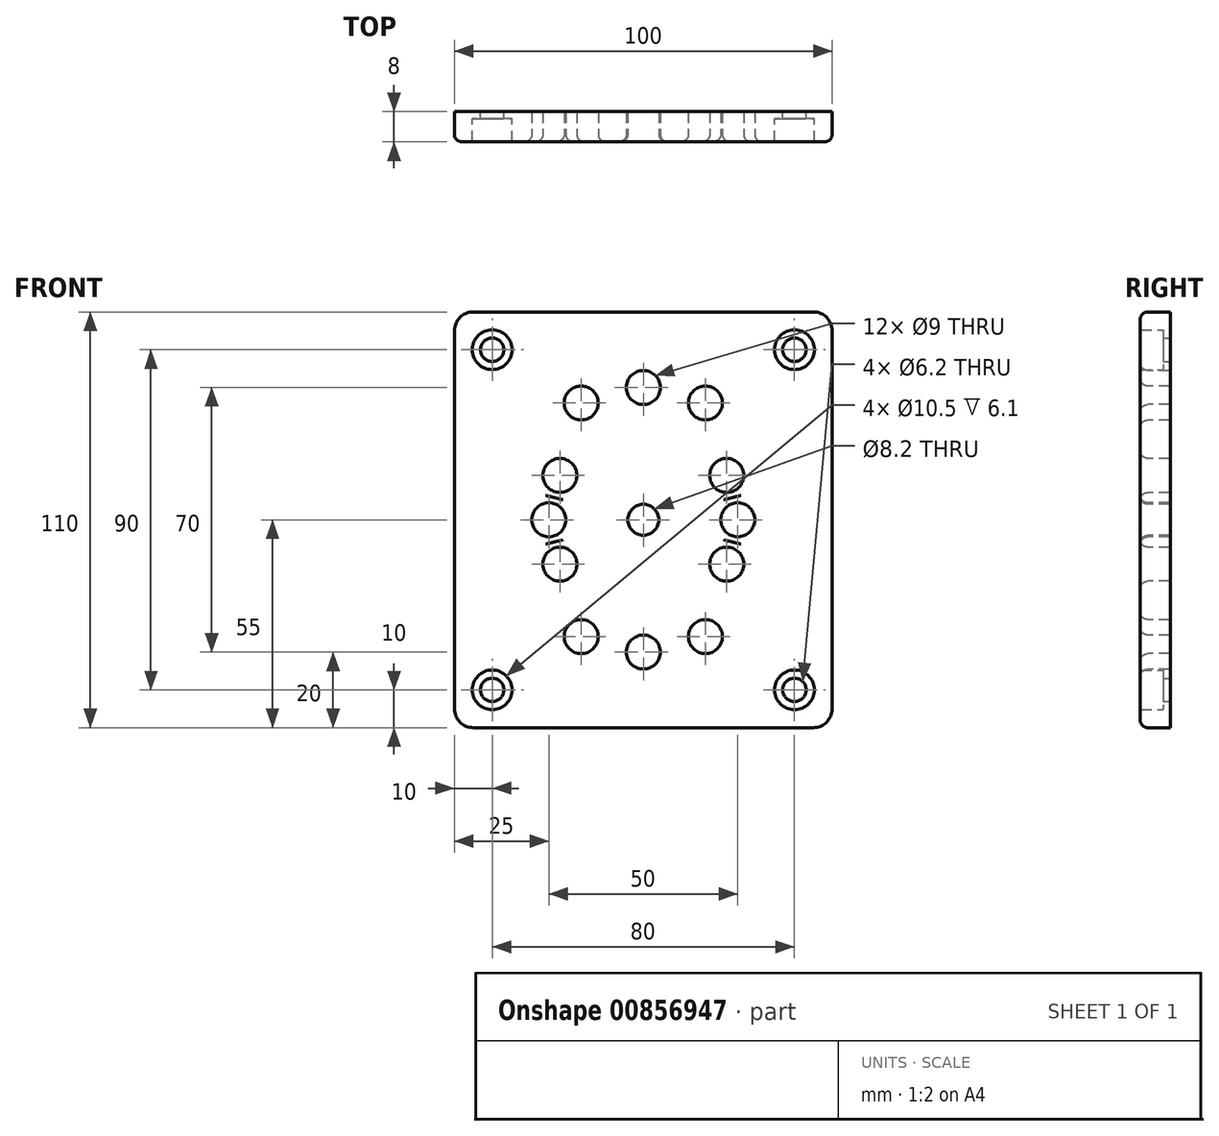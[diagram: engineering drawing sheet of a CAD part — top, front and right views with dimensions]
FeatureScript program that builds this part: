
annotation { "Feature Type Name" : "Feature", "Feature Type Description" : "" }
export const myFeature = defineFeature(function(context is Context, id is Id, definition is map)
    precondition{}
    {
        {
            var Q0;
            Q0=qCreatedBy(makeId("Front.planeOp"),FACE);
            var sketch = newSketch(context, id + "F0", { "sketchPlane" : qUnion([Q0])});
            skLineSegment(sketch, "E0.bottom", {"start": v(0, 0) * mm, "end": v(-100, 0) * mm});
            skLineSegment(sketch, "E0.top", {"start": v(0, 110) * mm, "end": v(-100, 110) * mm});
            skLineSegment(sketch, "E0.left", {"start": v(0, 0) * mm, "end": v(0, 110) * mm});
            skLineSegment(sketch, "E0.right", {"start": v(-100, 0) * mm, "end": v(-100, 110) * mm});
            skCircle(sketch, "E1", {"center": v(-50, 55) * mm, "radius": 4.1 * mm});
            skPoint(sketch, "E1.centerSnap0", {"position": v(-50, 0) * mm});
            skPoint(sketch, "E1.centerSnap1", {"position": v(-100, 55) * mm});
            skLineSegment(sketch, "E2", {"start": v(-50, 55) * mm, "end": v(-25, 55) * mm, "construction": true});
            skCircle(sketch, "E3", {"center": v(-50, 90) * mm, "radius": 4.5 * mm});
            skLineSegment(sketch, "E4", {"start": v(-50, 55) * mm, "end": v(-50, 90) * mm, "construction": true});
            skCircle(sketch, "E5.MirrorC", {"center": v(-50, 20) * mm, "radius": 4.5 * mm});
            skCircle(sketch, "E6", {"center": v(-25, 55) * mm, "radius": 4.5 * mm});
            skCircle(sketch, "E7.MirrorC", {"center": v(-75, 55) * mm, "radius": 4.5 * mm});
            skLineSegment(sketch, "E8", {"start": v(-50, 55) * mm, "end": v(-33.57, 85.9) * mm, "construction": true});
            skCircle(sketch, "E9", {"center": v(-33.57, 85.9) * mm, "radius": 4.5 * mm});
            skCircle(sketch, "E10.MirrorC", {"center": v(-33.57, 24.1) * mm, "radius": 4.5 * mm});
            skCircle(sketch, "E11.MirrorC", {"center": v(-66.43, 85.9) * mm, "radius": 4.5 * mm});
            skCircle(sketch, "E12.MirrorC", {"center": v(-66.43, 24.1) * mm, "radius": 4.5 * mm});
            skLineSegment(sketch, "E13", {"start": v(-50, 55) * mm, "end": v(-72.07, 43.26) * mm, "construction": true});
            skCircle(sketch, "E14", {"center": v(-72.07, 43.26) * mm, "radius": 4.5 * mm});
            skCircle(sketch, "E15.MirrorC", {"center": v(-27.93, 43.26) * mm, "radius": 4.5 * mm});
            skCircle(sketch, "E16.MirrorC", {"center": v(-27.93, 66.74) * mm, "radius": 4.5 * mm});
            skCircle(sketch, "E17.MirrorC", {"center": v(-72.07, 66.74) * mm, "radius": 4.5 * mm});
            skLineSegment(sketch, "E18", {"start": v(-50, 55) * mm, "end": v(-50, 100) * mm});
            skLineSegment(sketch, "E19", {"start": v(-50, 100) * mm, "end": v(-10, 100) * mm});
            skLineSegment(sketch, "E20", {"start": v(-10, 100) * mm, "end": v(-10, 10) * mm});
            skLineSegment(sketch, "E21.MirrorCS", {"start": v(-90, 100) * mm, "end": v(-90, 10) * mm});
            skSolve(sketch);
        }
        {
            var Q0;
            Q0=makeQuery(id+"F0.imprint","IMPRINT",FACE,{"disambiguationData":[TD([[makeQuery(id+"F0.imprint","IMPRINT",EDGE,{"derivedFrom":sQuery(id+"F0.wireOp",EDGE,"E0.bottom")}),-1.0]])]});
            extrude(context, id + "F1", {"entities" : qUnion([Q0]), "oppositeDirection" : true, "depth" : 8 * mm, "offsetDistance" : 25 * mm});
        }
        {
            var Q0;
            Q0=makeQuery(id+"F1.opExtrude","CAP_FACE",FACE,{"disambiguationData":[OSD([sQuery(id+"F0.wireOp",EDGE,"E0.bottom"),sQuery(id+"F0.wireOp",EDGE,"E0.top"),sQuery(id+"F0.wireOp",EDGE,"E0.left"),sQuery(id+"F0.wireOp",EDGE,"E0.right"),sQuery(id+"F0.wireOp",EDGE,"E1"),sQuery(id+"F0.wireOp",EDGE,"E3"),sQuery(id+"F0.wireOp",EDGE,"E5.MirrorC"),sQuery(id+"F0.wireOp",EDGE,"E6"),sQuery(id+"F0.wireOp",EDGE,"E7.MirrorC"),sQuery(id+"F0.wireOp",EDGE,"E9"),sQuery(id+"F0.wireOp",EDGE,"E10.MirrorC"),sQuery(id+"F0.wireOp",EDGE,"E11.MirrorC"),sQuery(id+"F0.wireOp",EDGE,"E12.MirrorC"),sQuery(id+"F0.wireOp",EDGE,"E14"),sQuery(id+"F0.wireOp",EDGE,"E15.MirrorC"),sQuery(id+"F0.wireOp",EDGE,"E16.MirrorC"),sQuery(id+"F0.wireOp",EDGE,"E17.MirrorC")])],"isStart":true});
            fillet(context, id + "F2", {"entities" : qUnion([Q0]), "tangentPropagation" : true, "radius" : 2 * mm, "defaultsChanged" : true, "vertexSettings" : [], "allowEdgeOverflow" : false});
        }
        {
            var Q0;
            Q0=sQuery(id+"F0.wireOp",VERTEX,"E21.MirrorCS.start");
            var Q1;
            Q1=sQuery(id+"F0.wireOp",VERTEX,"E21.MirrorCS.end");
            var Q2;
            Q2=sQuery(id+"F0.wireOp",VERTEX,"E20.end");
            var Q3;
            Q3=sQuery(id+"F0.wireOp",VERTEX,"E19.end");
            var Q4;
            Q4=makeQuery(id+"F1.opExtrude","SWEPT_BODY",BODY,{"disambiguationData":[OSD([sQuery(id+"F0.wireOp",EDGE,"E0.bottom"),sQuery(id+"F0.wireOp",EDGE,"E0.top"),sQuery(id+"F0.wireOp",EDGE,"E0.left"),sQuery(id+"F0.wireOp",EDGE,"E0.right"),sQuery(id+"F0.wireOp",EDGE,"E1"),sQuery(id+"F0.wireOp",EDGE,"E3"),sQuery(id+"F0.wireOp",EDGE,"E5.MirrorC"),sQuery(id+"F0.wireOp",EDGE,"E6"),sQuery(id+"F0.wireOp",EDGE,"E7.MirrorC"),sQuery(id+"F0.wireOp",EDGE,"E9"),sQuery(id+"F0.wireOp",EDGE,"E10.MirrorC"),sQuery(id+"F0.wireOp",EDGE,"E11.MirrorC"),sQuery(id+"F0.wireOp",EDGE,"E12.MirrorC"),sQuery(id+"F0.wireOp",EDGE,"E14"),sQuery(id+"F0.wireOp",EDGE,"E15.MirrorC"),sQuery(id+"F0.wireOp",EDGE,"E16.MirrorC"),sQuery(id+"F0.wireOp",EDGE,"E17.MirrorC")])]});
            hole(context, id + "F3", {"style" : HoleStyle.C_BORE, "endStyle" : HoleEndStyle.BLIND, "holeDiameter" : 6.2 * mm, "cBoreDiameter" : 10.5 * mm, "cBoreDepth" : 6.1 * mm, "majorDiameter" : 5 * mm, "holeDepth" : 8 * mm, "isTappedThrough" : true, "tappedDepth" : 9.9 * mm, "tapClearance" : 3, "locations" : qUnion([Q0, Q1, Q2, Q3]), "scope" : qUnion([Q4]), "startStyle" : HoleStartStyle.PART});
        }
        {
            var Q0;
            Q0=makeQuery(id+"F1.opExtrude","SWEPT_EDGE",EDGE,{"disambiguationData":[OSD([sQuery(id+"F0.wireOp",EDGE,"E0.bottom"),sQuery(id+"F0.wireOp",EDGE,"E0.left")])]});
            var Q1;
            Q1=makeQuery(id+"F1.opExtrude","SWEPT_EDGE",EDGE,{"disambiguationData":[OSD([sQuery(id+"F0.wireOp",EDGE,"E0.bottom"),sQuery(id+"F0.wireOp",EDGE,"E0.right")])]});
            var Q2;
            Q2=makeQuery(id+"F1.opExtrude","SWEPT_EDGE",EDGE,{"disambiguationData":[OSD([sQuery(id+"F0.wireOp",EDGE,"E0.top"),sQuery(id+"F0.wireOp",EDGE,"E0.right")])]});
            var Q3;
            Q3=makeQuery(id+"F1.opExtrude","SWEPT_EDGE",EDGE,{"disambiguationData":[OSD([sQuery(id+"F0.wireOp",EDGE,"E0.top"),sQuery(id+"F0.wireOp",EDGE,"E0.left")])]});
            fillet(context, id + "F4", {"entities" : qUnion([Q0, Q1, Q2, Q3]), "tangentPropagation" : true, "radius" : 5 * mm, "defaultsChanged" : false, "vertexSettings" : [], "allowEdgeOverflow" : false});
        }
    });
